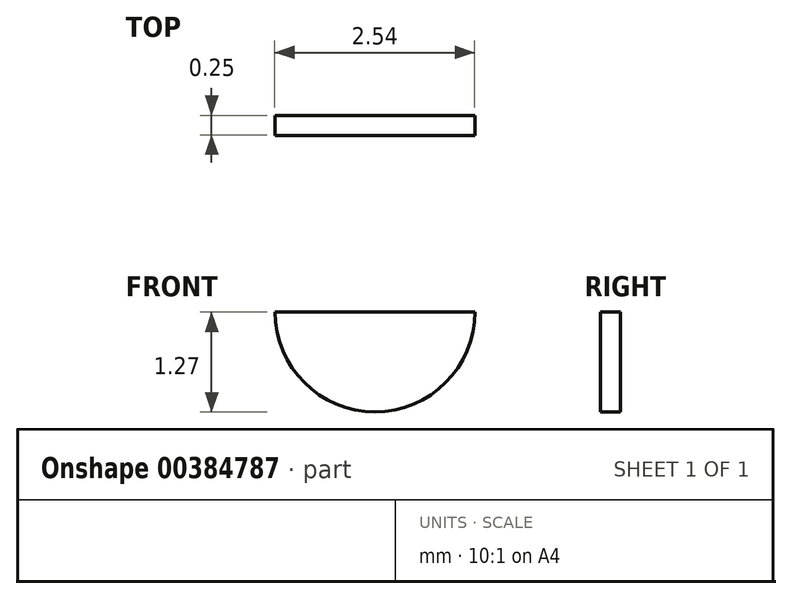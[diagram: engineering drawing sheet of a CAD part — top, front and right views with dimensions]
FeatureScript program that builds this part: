
annotation { "Feature Type Name" : "Feature", "Feature Type Description" : "" }
export const myFeature = defineFeature(function(context is Context, id is Id, definition is map)
    precondition{}
    {
        {
            var Q0;
            Q0=qCreatedBy(makeId("Front.planeOp"),FACE);
            var sketch = newSketch(context, id + "F0", { "sketchPlane" : qUnion([Q0])});
            skLineSegment(sketch, "E0", {"start": v(-43.2, 31.32) * mm, "end": v(-40.66, 31.32) * mm});
            skLineSegment(sketch, "E1", {"start": v(-40.66, 31.32) * mm, "end": v(-41.93, 31.32) * mm});
            skArc(sketch, "E2", {"start": v(-43.2, 31.32) * mm, "mid": v(-41.93, 30.05) * mm, "end": v(-40.66, 31.32) * mm});
            skSolve(sketch);
        }
        {
            var Q0;
            Q0=makeQuery(id+"F0.imprint","IMPRINT",FACE,{"disambiguationData":[TD([[makeQuery(id+"F0.imprint","IMPRINT",EDGE,{"derivedFrom":sQuery(id+"F0.wireOp",EDGE,"E0")}),-1.0]])]});
            extrude(context, id + "F1", {"entities" : qUnion([Q0]), "depth" : 0.25 * mm});
        }
    });
